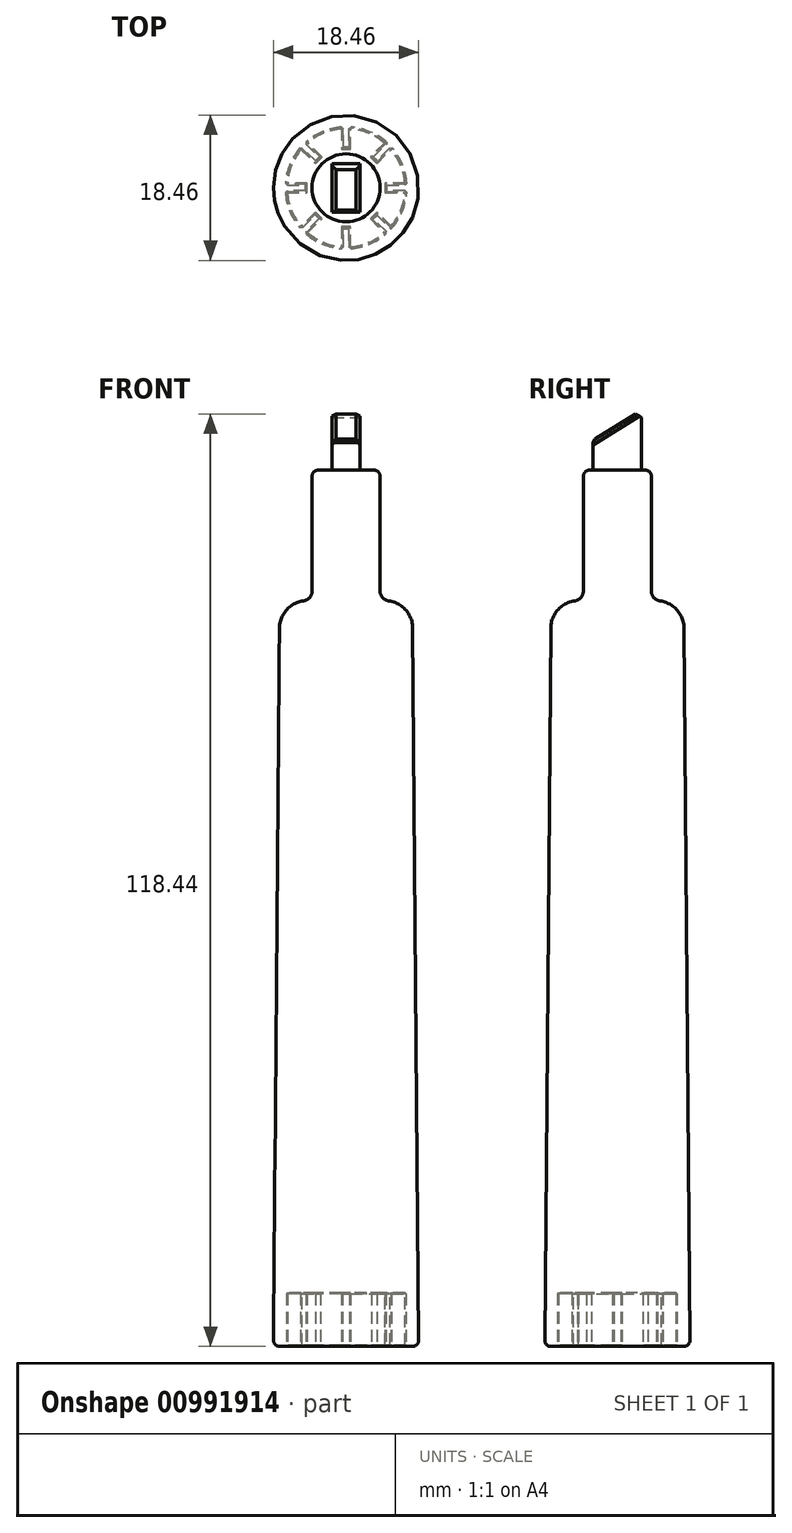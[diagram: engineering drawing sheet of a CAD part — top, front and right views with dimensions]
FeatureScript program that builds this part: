
annotation { "Feature Type Name" : "Feature", "Feature Type Description" : "" }
export const myFeature = defineFeature(function(context is Context, id is Id, definition is map)
    precondition{}
    {
        {
            var Q0;
            Q0=qCreatedBy(makeId("Front.planeOp"),FACE);
            var sketch = newSketch(context, id + "F0", { "sketchPlane" : qUnion([Q0])});
            skLineSegment(sketch, "E0", {"start": v(0, 0) * mm, "end": v(0, 111.3) * mm, "construction": true});
            skLineSegment(sketch, "E1", {"start": v(9.23, 0) * mm, "end": v(8.46, 91.26) * mm});
            skLineSegment(sketch, "E2", {"start": v(4.32, 111.3) * mm, "end": v(4.32, 95.96) * mm});
            skArc(sketch, "E3", {"start": v(8.46, 91.26) * mm, "mid": v(7.58, 93.55) * mm, "end": v(5.42, 94.7) * mm});
            skLineSegment(sketch, "E4", {"start": v(0, 111.3) * mm, "end": v(4.32, 111.3) * mm});
            skLineSegment(sketch, "E5", {"start": v(0, 0) * mm, "end": v(9.23, 0) * mm});
            skPoint(sketch, "E6.visualSharp", {"position": v(4.32, 94.67) * mm});
            skArc(sketch, "E6.filletArc", {"start": v(4.32, 95.96) * mm, "mid": v(4.63, 95.12) * mm, "end": v(5.42, 94.7) * mm});
            skLineSegment(sketch, "E7", {"start": v(0, 111.3) * mm, "end": v(0, 0) * mm});
            skSolve(sketch);
        }
        {
            var Q0;
            Q0=qSketchRegion(id+"F0",true);
            var Q1;
            Q1=sQuery(id+"F0.wireOp",EDGE,"E0");
            revolve(context, id + "F1", {"entities" : qUnion([Q0]), "axis" : qUnion([Q1]), "revolveType" : RevolveType.FULL});
        }
        {
            var Q0;
            Q0=makeQuery(id+"F1.opRevolve","SWEPT_EDGE",EDGE,{"disambiguationData":[OSD([sQuery(id+"F0.wireOp",EDGE,"E2"),sQuery(id+"F0.wireOp",EDGE,"E4")])]});
            var Q1;
            Q1=makeQuery(id+"F1.opRevolve","SWEPT_EDGE",EDGE,{"disambiguationData":[OSD([sQuery(id+"F0.wireOp",EDGE,"E1"),sQuery(id+"F0.wireOp",EDGE,"E5")])]});
            fillet(context, id + "F2", {"entities" : qUnion([Q0, Q1]), "radius" : 0.76 * mm, "tangentPropagation" : true, "allowEdgeOverflow" : false});
        }
        {
            var Q0;
            Q0=makeQuery(id+"F1.opRevolve","SWEPT_FACE",FACE,{"disambiguationData":[OSD([sQuery(id+"F0.wireOp",EDGE,"E4")])]});
            var sketch = newSketch(context, id + "F3", { "sketchPlane" : qUnion([Q0])});
            skLineSegment(sketch, "E8.bottom", {"start": v(-1.78, 3.08) * mm, "end": v(1.78, 3.08) * mm});
            skLineSegment(sketch, "E8.top", {"start": v(-1.78, -3.08) * mm, "end": v(1.78, -3.08) * mm});
            skLineSegment(sketch, "E8.left", {"start": v(-1.78, 3.08) * mm, "end": v(-1.78, -3.08) * mm});
            skLineSegment(sketch, "E8.right", {"start": v(1.78, 3.08) * mm, "end": v(1.78, -3.08) * mm});
            skSolve(sketch);
        }
        {
            var Q0;
            Q0=qSketchRegion(id+"F3",true);
            extrude(context, id + "F4", {"entities" : qUnion([Q0]), "operationType" : NewBodyOperationType.ADD, "depth" : 7.62 * mm});
        }
        {
            var Q0;
            Q0=makeQuery(id+"F4.opExtrude","SWEPT_FACE",FACE,{"disambiguationData":[OSD([sQuery(id+"F3.wireOp",EDGE,"E8.right")])]});
            var sketch = newSketch(context, id + "F5", { "sketchPlane" : qUnion([Q0])});
            skLineSegment(sketch, "E9", {"start": v(-3.08, 118.92) * mm, "end": v(-3.08, 115.11) * mm});
            skLineSegment(sketch, "E10", {"start": v(-3.08, 115.11) * mm, "end": v(3.08, 118.92) * mm});
            skLineSegment(sketch, "E11", {"start": v(3.08, 118.92) * mm, "end": v(-3.08, 118.92) * mm});
            skSolve(sketch);
        }
        {
            var Q0;
            Q0=qSketchRegion(id+"F5",true);
            extrude(context, id + "F6", {"entities" : qUnion([Q0]), "operationType" : NewBodyOperationType.REMOVE, "endBound" : BoundingType.UP_TO_NEXT, "oppositeDirection" : true, "depth" : 25.4 * mm});
        }
        {
            var Q0;
            Q0=makeQuery(id+"F6.boolean.opBoolean","COPY",FACE,{"derivedFrom":makeQuery(id+"F6.opExtrude","SWEPT_FACE",FACE,{"disambiguationData":[OSD([sQuery(id+"F5.wireOp",EDGE,"E10")])]})});
            chamfer(context, id + "F7", {"entities" : qUnion([Q0]), "width" : 0.5 * mm, "tangentPropagation" : true});
        }
        {
            var Q0;
            Q0=makeQuery(id+"F1.opRevolve","SWEPT_FACE",FACE,{"disambiguationData":[OSD([sQuery(id+"F0.wireOp",EDGE,"E5")])]});
            var sketch = newSketch(context, id + "F8", { "sketchPlane" : qUnion([Q0])});
            skArc(sketch, "E12", {"start": v(-7.6, -0.46) * mm, "mid": v(-7.04, -2.92) * mm, "end": v(-5.7, -5.06) * mm});
            skLineSegment(sketch, "E13", {"start": v(-7.6, -0.46) * mm, "end": v(-5.07, -0.46) * mm});
            skLineSegment(sketch, "E14", {"start": v(-5.07, -0.46) * mm, "end": v(-5.07, 0.46) * mm});
            skLineSegment(sketch, "E15", {"start": v(-5.07, 0.46) * mm, "end": v(-7.6, 0.46) * mm});
            skLineSegment(sketch, "E16", {"start": v(7.62, 0) * mm, "end": v(-7.6, 0) * mm, "construction": true});
            skLineSegment(sketch, "E17.1.0", {"start": v(-3.26, 3.9) * mm, "end": v(-5.06, 5.7) * mm});
            skLineSegment(sketch, "E17.1.1", {"start": v(-3.9, 3.26) * mm, "end": v(-3.26, 3.9) * mm});
            skLineSegment(sketch, "E17.1.2", {"start": v(-5.7, 5.06) * mm, "end": v(-3.9, 3.26) * mm});
            skLineSegment(sketch, "E17.2.0", {"start": v(0.46, 5.07) * mm, "end": v(0.46, 7.6) * mm});
            skLineSegment(sketch, "E17.2.1", {"start": v(-0.46, 5.07) * mm, "end": v(0.46, 5.07) * mm});
            skLineSegment(sketch, "E17.2.2", {"start": v(-0.46, 7.6) * mm, "end": v(-0.46, 5.07) * mm});
            skLineSegment(sketch, "E17.3.0", {"start": v(3.9, 3.26) * mm, "end": v(5.7, 5.06) * mm});
            skLineSegment(sketch, "E17.3.1", {"start": v(3.26, 3.9) * mm, "end": v(3.9, 3.26) * mm});
            skLineSegment(sketch, "E17.3.2", {"start": v(5.06, 5.7) * mm, "end": v(3.26, 3.9) * mm});
            skLineSegment(sketch, "E17.4.0", {"start": v(5.07, -0.46) * mm, "end": v(7.6, -0.46) * mm});
            skLineSegment(sketch, "E17.4.1", {"start": v(5.07, 0.46) * mm, "end": v(5.07, -0.46) * mm});
            skLineSegment(sketch, "E17.4.2", {"start": v(7.6, 0.46) * mm, "end": v(5.07, 0.46) * mm});
            skLineSegment(sketch, "E17.5.0", {"start": v(3.26, -3.9) * mm, "end": v(5.06, -5.7) * mm});
            skLineSegment(sketch, "E17.5.1", {"start": v(3.9, -3.26) * mm, "end": v(3.26, -3.9) * mm});
            skLineSegment(sketch, "E17.5.2", {"start": v(5.7, -5.06) * mm, "end": v(3.9, -3.26) * mm});
            skLineSegment(sketch, "E17.6.0", {"start": v(-0.46, -5.07) * mm, "end": v(-0.46, -7.6) * mm});
            skLineSegment(sketch, "E17.6.1", {"start": v(0.46, -5.07) * mm, "end": v(-0.46, -5.07) * mm});
            skLineSegment(sketch, "E17.6.2", {"start": v(0.46, -7.6) * mm, "end": v(0.46, -5.07) * mm});
            skLineSegment(sketch, "E17.7.0", {"start": v(-3.9, -3.26) * mm, "end": v(-5.7, -5.06) * mm});
            skLineSegment(sketch, "E17.7.1", {"start": v(-3.26, -3.9) * mm, "end": v(-3.9, -3.26) * mm});
            skLineSegment(sketch, "E17.7.2", {"start": v(-5.06, -5.7) * mm, "end": v(-3.26, -3.9) * mm});
            skLineSegment(sketch, "E17.anchor1", {"start": v(0, 0) * mm, "end": v(-7.6, 0.46) * mm, "construction": true});
            skLineSegment(sketch, "E17.anchor2", {"start": v(0, 0) * mm, "end": v(-5.7, -5.06) * mm, "construction": true});
            skArc(sketch, "E18.trimOffspring", {"start": v(-0.46, 7.6) * mm, "mid": v(-2.92, 7.04) * mm, "end": v(-5.06, 5.7) * mm});
            skArc(sketch, "E19.trimOffspring", {"start": v(-5.7, 5.06) * mm, "mid": v(-7.04, 2.92) * mm, "end": v(-7.6, 0.46) * mm});
            skArc(sketch, "E20.trimOffspring", {"start": v(5.06, 5.7) * mm, "mid": v(2.92, 7.04) * mm, "end": v(0.46, 7.6) * mm});
            skArc(sketch, "E21.trimOffspring", {"start": v(7.6, 0.46) * mm, "mid": v(7.04, 2.92) * mm, "end": v(5.7, 5.06) * mm});
            skArc(sketch, "E22.trimOffspring", {"start": v(5.7, -5.06) * mm, "mid": v(7.04, -2.92) * mm, "end": v(7.6, -0.46) * mm});
            skArc(sketch, "E23.trimOffspring", {"start": v(0.46, -7.6) * mm, "mid": v(2.92, -7.04) * mm, "end": v(5.06, -5.7) * mm});
            skArc(sketch, "E24.trimOffspring", {"start": v(-5.06, -5.7) * mm, "mid": v(-2.92, -7.04) * mm, "end": v(-0.46, -7.6) * mm});
            skSolve(sketch);
        }
        {
            var Q0;
            Q0=qSketchRegion(id+"F8",true);
            extrude(context, id + "F9", {"entities" : qUnion([Q0]), "operationType" : NewBodyOperationType.REMOVE, "oppositeDirection" : true, "depth" : 6.8 * mm});
        }
        {
            var Q0;
            Q0=makeQuery(id+"F1.opRevolve","SWEPT_FACE",FACE,{"disambiguationData":[OSD([sQuery(id+"F0.wireOp",EDGE,"E5")])]});
            var Q1;
            Q1=makeQuery(id+"F9.boolean.opBoolean","COPY",FACE,{"derivedFrom":makeQuery(id+"F9.opExtrude","CAP_FACE",FACE,{"disambiguationData":[OSD([sQuery(id+"F8.wireOp",EDGE,"E12"),sQuery(id+"F8.wireOp",EDGE,"E13"),sQuery(id+"F8.wireOp",EDGE,"E14"),sQuery(id+"F8.wireOp",EDGE,"E15"),sQuery(id+"F8.wireOp",EDGE,"E17.1.0"),sQuery(id+"F8.wireOp",EDGE,"E17.1.1"),sQuery(id+"F8.wireOp",EDGE,"E17.1.2"),sQuery(id+"F8.wireOp",EDGE,"E17.2.0"),sQuery(id+"F8.wireOp",EDGE,"E17.2.1"),sQuery(id+"F8.wireOp",EDGE,"E17.2.2"),sQuery(id+"F8.wireOp",EDGE,"E17.3.0"),sQuery(id+"F8.wireOp",EDGE,"E17.3.1"),sQuery(id+"F8.wireOp",EDGE,"E17.3.2"),sQuery(id+"F8.wireOp",EDGE,"E17.4.0"),sQuery(id+"F8.wireOp",EDGE,"E17.4.1"),sQuery(id+"F8.wireOp",EDGE,"E17.4.2"),sQuery(id+"F8.wireOp",EDGE,"E17.5.0"),sQuery(id+"F8.wireOp",EDGE,"E17.5.1"),sQuery(id+"F8.wireOp",EDGE,"E17.5.2"),sQuery(id+"F8.wireOp",EDGE,"E17.6.0"),sQuery(id+"F8.wireOp",EDGE,"E17.6.1"),sQuery(id+"F8.wireOp",EDGE,"E17.6.2"),sQuery(id+"F8.wireOp",EDGE,"E17.7.0"),sQuery(id+"F8.wireOp",EDGE,"E17.7.1"),sQuery(id+"F8.wireOp",EDGE,"E17.7.2"),sQuery(id+"F8.wireOp",EDGE,"E18.trimOffspring"),sQuery(id+"F8.wireOp",EDGE,"E19.trimOffspring"),sQuery(id+"F8.wireOp",EDGE,"E20.trimOffspring"),sQuery(id+"F8.wireOp",EDGE,"E21.trimOffspring"),sQuery(id+"F8.wireOp",EDGE,"E22.trimOffspring"),sQuery(id+"F8.wireOp",EDGE,"E23.trimOffspring"),sQuery(id+"F8.wireOp",EDGE,"E24.trimOffspring")])],"isStart":false})});
            var Q2;
            Q2=makeQuery(id+"F9.boolean.opBoolean","COPY",FACE,{"derivedFrom":makeQuery(id+"F9.opExtrude","SWEPT_FACE",FACE,{"disambiguationData":[OSD([sQuery(id+"F8.wireOp",EDGE,"E12")])]})});
            var Q3;
            Q3=makeQuery(id+"F9.boolean.opBoolean","COPY",FACE,{"derivedFrom":makeQuery(id+"F9.opExtrude","SWEPT_FACE",FACE,{"disambiguationData":[OSD([sQuery(id+"F8.wireOp",EDGE,"E24.trimOffspring")])]})});
            var Q4;
            Q4=makeQuery(id+"F9.boolean.opBoolean","COPY",EDGE,{"derivedFrom":makeQuery(id+"F9.opExtrude","SWEPT_EDGE",EDGE,{"disambiguationData":[OSD([sQuery(id+"F8.wireOp",EDGE,"E17.6.2"),sQuery(id+"F8.wireOp",EDGE,"E23.trimOffspring")])]})});
            var Q5;
            Q5=makeQuery(id+"F9.boolean.opBoolean","COPY",FACE,{"derivedFrom":makeQuery(id+"F9.opExtrude","SWEPT_FACE",FACE,{"disambiguationData":[OSD([sQuery(id+"F8.wireOp",EDGE,"E22.trimOffspring")])]})});
            var Q6;
            Q6=makeQuery(id+"F9.boolean.opBoolean","COPY",EDGE,{"derivedFrom":makeQuery(id+"F9.opExtrude","SWEPT_EDGE",EDGE,{"disambiguationData":[OSD([sQuery(id+"F8.wireOp",EDGE,"E17.4.2"),sQuery(id+"F8.wireOp",EDGE,"E21.trimOffspring")])]})});
            var Q7;
            Q7=makeQuery(id+"F9.boolean.opBoolean","COPY",FACE,{"derivedFrom":makeQuery(id+"F9.opExtrude","SWEPT_FACE",FACE,{"disambiguationData":[OSD([sQuery(id+"F8.wireOp",EDGE,"E20.trimOffspring")])]})});
            var Q8;
            Q8=makeQuery(id+"F9.boolean.opBoolean","COPY",FACE,{"derivedFrom":makeQuery(id+"F9.opExtrude","SWEPT_FACE",FACE,{"disambiguationData":[OSD([sQuery(id+"F8.wireOp",EDGE,"E18.trimOffspring")])]})});
            var Q9;
            Q9=makeQuery(id+"F9.boolean.opBoolean","COPY",FACE,{"derivedFrom":makeQuery(id+"F9.opExtrude","SWEPT_FACE",FACE,{"disambiguationData":[OSD([sQuery(id+"F8.wireOp",EDGE,"E19.trimOffspring")])]})});
            chamfer(context, id + "F10", {"entities" : qUnion([Q0, Q1, Q2, Q3, Q4, Q5, Q6, Q7, Q8, Q9]), "width" : 0.13 * mm, "tangentPropagation" : true});
        }
    });
